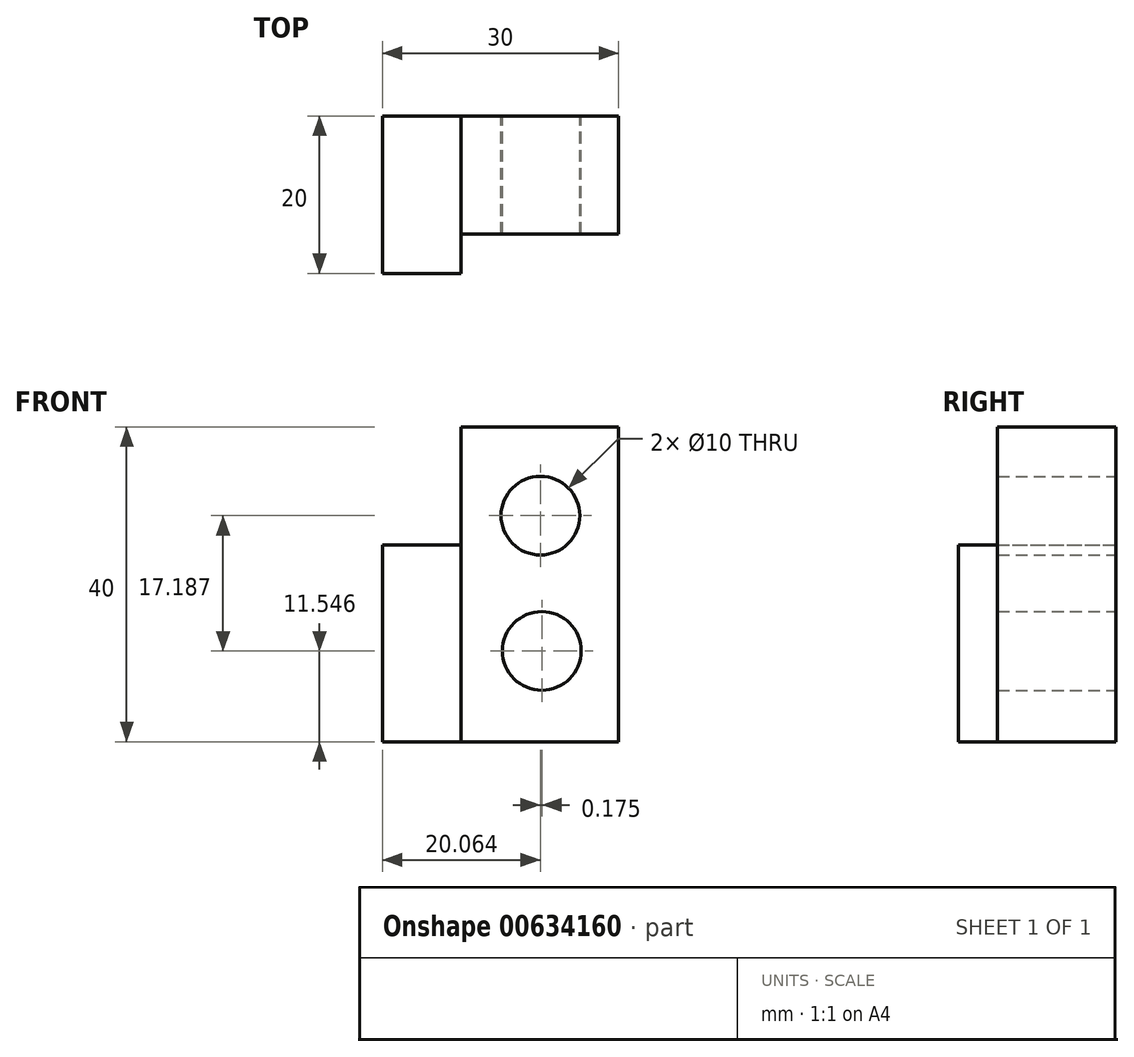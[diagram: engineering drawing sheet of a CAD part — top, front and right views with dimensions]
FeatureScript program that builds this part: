
annotation { "Feature Type Name" : "Feature", "Feature Type Description" : "" }
export const myFeature = defineFeature(function(context is Context, id is Id, definition is map)
    precondition{}
    {
        {
            var Q0;
            Q0=qCreatedBy(makeId("Front.planeOp"),FACE);
            var sketch = newSketch(context, id + "F0", { "sketchPlane" : qUnion([Q0])});
            skLineSegment(sketch, "E0.bottom", {"start": v(-10.24, 20.1) * mm, "end": v(9.76, 20.1) * mm});
            skLineSegment(sketch, "E0.top", {"start": v(-10.24, -19.9) * mm, "end": v(9.76, -19.9) * mm});
            skLineSegment(sketch, "E0.left", {"start": v(-10.24, 20.1) * mm, "end": v(-10.24, -19.9) * mm});
            skLineSegment(sketch, "E0.right", {"start": v(9.76, 20.1) * mm, "end": v(9.76, -19.9) * mm});
            skCircle(sketch, "E1", {"center": v(-0.18, 8.82) * mm, "radius": 5 * mm});
            skCircle(sketch, "E2", {"center": v(0, -8.36) * mm, "radius": 5 * mm});
            skSolve(sketch);
        }
        {
            var Q0;
            Q0 = qSketchRegion(id + "F0", true);
            extrude(context, id + "F1", {"entities" : qUnion([Q0]), "depth" : 15 * mm, "offsetDistance" : 25 * mm});
        }
        {
            var Q0;
            Q0=qCreatedBy(makeId("Front.planeOp"),FACE);
            var sketch = newSketch(context, id + "F2", { "sketchPlane" : qUnion([Q0])});
            skLineSegment(sketch, "E3.bottom", {"start": v(-10.24, -19.9) * mm, "end": v(-20.24, -19.9) * mm});
            skLineSegment(sketch, "E3.top", {"start": v(-10.24, 5.1) * mm, "end": v(-20.24, 5.1) * mm});
            skLineSegment(sketch, "E3.left", {"start": v(-10.24, -19.9) * mm, "end": v(-10.24, 5.1) * mm});
            skLineSegment(sketch, "E3.right", {"start": v(-20.24, -19.9) * mm, "end": v(-20.24, 5.1) * mm});
            skSolve(sketch);
        }
        {
            var Q0;
            Q0=makeQuery(id+"F2.imprint","IMPRINT",FACE,{"disambiguationData":[TD([[makeQuery(id+"F2.imprint","IMPRINT",EDGE,{"derivedFrom":sQuery(id+"F2.wireOp",EDGE,"E3.bottom")}),-1.0]])]});
            extrude(context, id + "F3", {"entities" : qUnion([Q0]), "operationType" : NewBodyOperationType.ADD, "depth" : 20 * mm, "offsetDistance" : 25 * mm});
        }
    });
